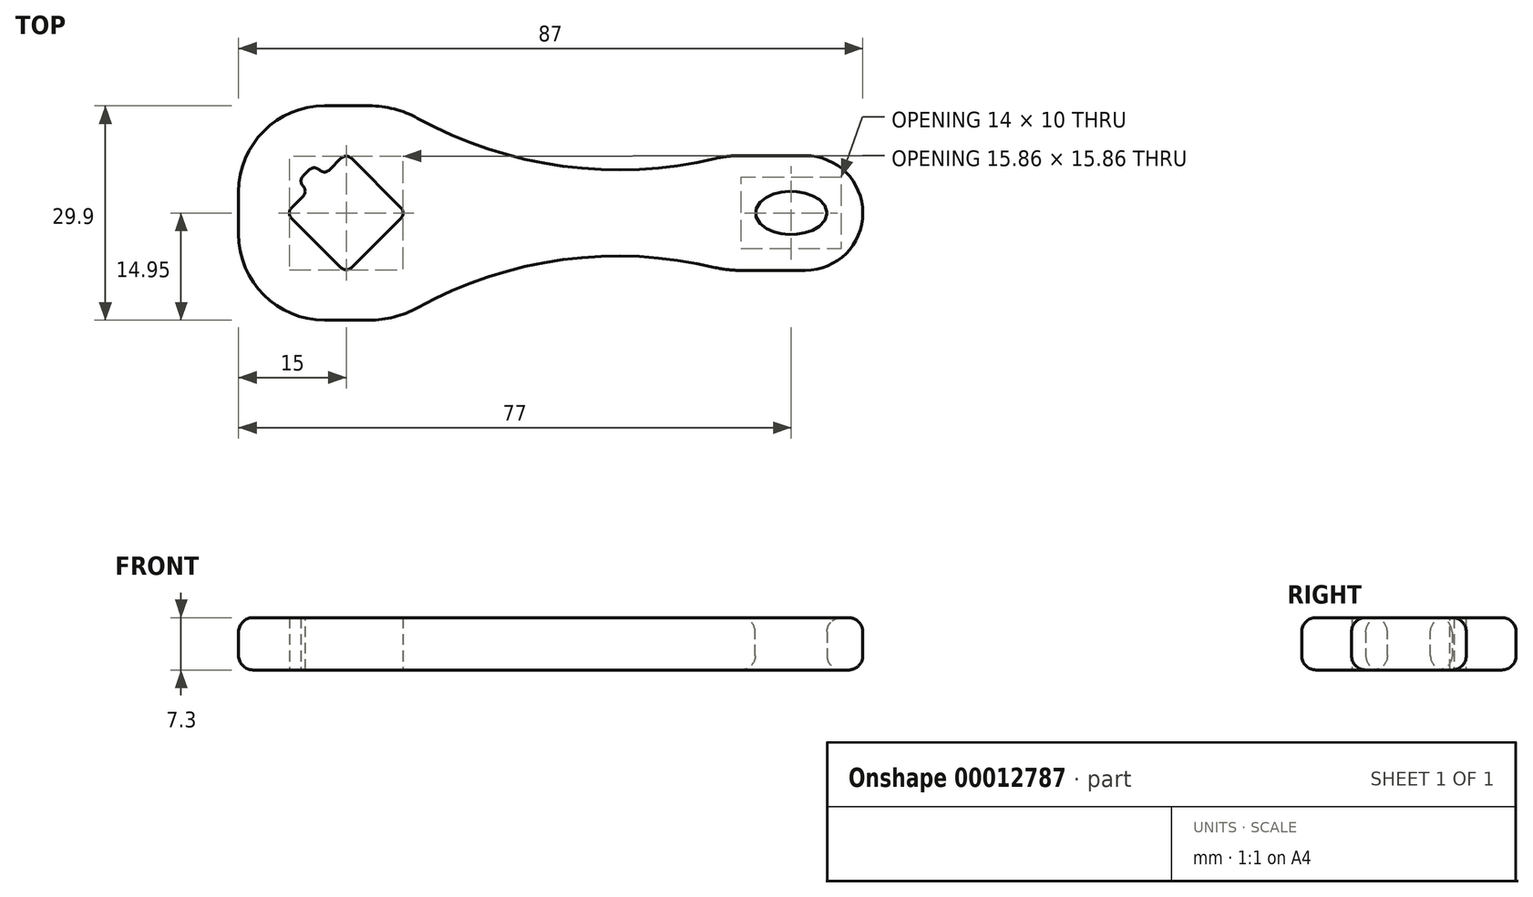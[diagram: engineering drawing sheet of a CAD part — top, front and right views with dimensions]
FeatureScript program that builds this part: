
annotation { "Feature Type Name" : "Feature", "Feature Type Description" : "" }
export const myFeature = defineFeature(function(context is Context, id is Id, definition is map)
    precondition{}
    {
        {
            var Q0;
            Q0=qCreatedBy(makeId("Top.planeOp"),FACE);
            var sketch = newSketch(context, id + "F0", { "sketchPlane" : qUnion([Q0])});
            skLineSegment(sketch, "E0", {"start": v(0, 8.34) * mm, "end": v(0, -8.34) * mm, "construction": true});
            skLineSegment(sketch, "E1", {"start": v(0, 8.34) * mm, "end": v(8.34, 0) * mm});
            skLineSegment(sketch, "E2", {"start": v(8.34, 0) * mm, "end": v(0, -8.34) * mm});
            skLineSegment(sketch, "E3", {"start": v(0, -8.34) * mm, "end": v(-8.34, 0) * mm});
            skLineSegment(sketch, "E4", {"start": v(-8.34, 0) * mm, "end": v(-5.3, 3.04) * mm});
            skLineSegment(sketch, "E5", {"start": v(-5.3, 3.04) * mm, "end": v(-6.72, 4.45) * mm});
            skLineSegment(sketch, "E6", {"start": v(-6.72, 4.45) * mm, "end": v(-4.45, 6.72) * mm});
            skLineSegment(sketch, "E7", {"start": v(-4.45, 6.72) * mm, "end": v(-3.04, 5.3) * mm});
            skLineSegment(sketch, "E8", {"start": v(-3.04, 5.3) * mm, "end": v(0, 8.34) * mm});
            skSolve(sketch);
        }
        {
            var Q0;
            Q0=qCreatedBy(makeId("Top.planeOp"),FACE);
            var sketch = newSketch(context, id + "F1", { "sketchPlane" : qUnion([Q0])});
            skLineSegment(sketch, "E9", {"start": v(7, 14.95) * mm, "end": v(-3, 14.95) * mm});
            skLineSegment(sketch, "E10", {"start": v(-15, 2.95) * mm, "end": v(-15, -2.95) * mm});
            skLineSegment(sketch, "E11", {"start": v(-3, -14.95) * mm, "end": v(7, -14.95) * mm});
            skPoint(sketch, "E12.visualSharp", {"position": v(-15, 14.95) * mm});
            skArc(sketch, "E12.filletArc", {"start": v(-3, 14.95) * mm, "mid": v(-11.49, 11.44) * mm, "end": v(-15, 2.95) * mm});
            skPoint(sketch, "E13.visualSharp", {"position": v(-15, -14.95) * mm});
            skArc(sketch, "E13.filletArc", {"start": v(-15, -2.95) * mm, "mid": v(-11.49, -11.44) * mm, "end": v(-3, -14.95) * mm});
            skLineSegment(sketch, "E14", {"start": v(0, 0) * mm, "end": v(64, 0) * mm, "construction": true});
            skLineSegment(sketch, "E15", {"start": v(0, 0) * mm, "end": v(-15, 0) * mm, "construction": true});
            skLineSegment(sketch, "E16", {"start": v(53, 8) * mm, "end": v(64, 8) * mm});
            skLineSegment(sketch, "E17", {"start": v(53, -8) * mm, "end": v(64, -8) * mm});
            skArc(sketch, "E18", {"start": v(64, 8) * mm, "mid": v(72, 0) * mm, "end": v(64, -8) * mm});
            skArc(sketch, "E19", {"start": v(7, 14.95) * mm, "mid": v(29.27, 6.66) * mm, "end": v(53, 8) * mm});
            skArc(sketch, "E20", {"start": v(53, -8) * mm, "mid": v(29.27, -6.66) * mm, "end": v(7, -14.95) * mm});
            skEllipse(sketch, "E21", {"center": v(62, 0) * mm, "majorRadius": 5 * mm, "minorRadius": 3 * mm, "majorAxis": v(1, 0)});
            skLineSegment(sketch, "E22", {"start": v(62, 8) * mm, "end": v(62, 3) * mm, "construction": true});
            skLineSegment(sketch, "E23", {"start": v(67, 0) * mm, "end": v(72, 0) * mm, "construction": true});
            skSolve(sketch);
        }
        {
            var Q0;
            Q0=qSketchRegion(id+"F0",true);
            extrude(context, id + "F2", {"entities" : qUnion([Q0]), "depth" : 10 * mm});
        }
        {
            var Q0;
            Q0=qSketchRegion(id+"F1",true);
            extrude(context, id + "F3", {"entities" : qUnion([Q0]), "depth" : 7.3 * mm});
        }
        {
            var Q0;
            Q0=makeQuery(id+"F2.opExtrude","SWEPT_EDGE",EDGE,{"disambiguationData":[OSD([sQuery(id+"F0.wireOp",EDGE,"E2"),sQuery(id+"F0.wireOp",EDGE,"E3")])]});
            var Q1;
            Q1=makeQuery(id+"F2.opExtrude","SWEPT_EDGE",EDGE,{"disambiguationData":[OSD([sQuery(id+"F0.wireOp",EDGE,"E3"),sQuery(id+"F0.wireOp",EDGE,"E4")])]});
            var Q2;
            Q2=makeQuery(id+"F2.opExtrude","SWEPT_EDGE",EDGE,{"disambiguationData":[OSD([sQuery(id+"F0.wireOp",EDGE,"E1"),sQuery(id+"F0.wireOp",EDGE,"E2")])]});
            var Q3;
            Q3=makeQuery(id+"F2.opExtrude","SWEPT_EDGE",EDGE,{"disambiguationData":[OSD([sQuery(id+"F0.wireOp",EDGE,"E1"),sQuery(id+"F0.wireOp",EDGE,"E8")])]});
            var Q4;
            Q4=makeQuery(id+"F2.opExtrude","SWEPT_EDGE",EDGE,{"disambiguationData":[OSD([sQuery(id+"F0.wireOp",EDGE,"E6"),sQuery(id+"F0.wireOp",EDGE,"E7")])]});
            var Q5;
            Q5=makeQuery(id+"F2.opExtrude","SWEPT_EDGE",EDGE,{"disambiguationData":[OSD([sQuery(id+"F0.wireOp",EDGE,"E5"),sQuery(id+"F0.wireOp",EDGE,"E6")])]});
            var Q6;
            Q6=makeQuery(id+"F2.opExtrude","SWEPT_EDGE",EDGE,{"disambiguationData":[OSD([sQuery(id+"F0.wireOp",EDGE,"E4"),sQuery(id+"F0.wireOp",EDGE,"E5")])]});
            var Q7;
            Q7=makeQuery(id+"F2.opExtrude","SWEPT_EDGE",EDGE,{"disambiguationData":[OSD([sQuery(id+"F0.wireOp",EDGE,"E7"),sQuery(id+"F0.wireOp",EDGE,"E8")])]});
            fillet(context, id + "F4", {"entities" : qUnion([Q0, Q1, Q2, Q3, Q4, Q5, Q6, Q7]), "radius" : 1 * mm, "allowEdgeOverflow" : false});
        }
        {
            var Q0;
            Q0=makeQuery(id+"F2.opExtrude","SWEPT_BODY",BODY,{"disambiguationData":[OSD([sQuery(id+"F0.wireOp",EDGE,"E1"),sQuery(id+"F0.wireOp",EDGE,"E2"),sQuery(id+"F0.wireOp",EDGE,"E3"),sQuery(id+"F0.wireOp",EDGE,"E4"),sQuery(id+"F0.wireOp",EDGE,"E5"),sQuery(id+"F0.wireOp",EDGE,"E6"),sQuery(id+"F0.wireOp",EDGE,"E7"),sQuery(id+"F0.wireOp",EDGE,"E8")])]});
            var Q1;
            Q1=makeQuery(id+"F3.opExtrude","SWEPT_BODY",BODY,{"disambiguationData":[OSD([sQuery(id+"F1.wireOp",EDGE,"E9"),sQuery(id+"F1.wireOp",EDGE,"E10"),sQuery(id+"F1.wireOp",EDGE,"E11"),sQuery(id+"F1.wireOp",EDGE,"E12.filletArc"),sQuery(id+"F1.wireOp",EDGE,"E13.filletArc"),sQuery(id+"F1.wireOp",EDGE,"E16"),sQuery(id+"F1.wireOp",EDGE,"E17"),sQuery(id+"F1.wireOp",EDGE,"E18"),sQuery(id+"F1.wireOp",EDGE,"E19"),sQuery(id+"F1.wireOp",EDGE,"E20"),sQuery(id+"F1.wireOp",EDGE,"E21")])]});
            booleanBodies(context, id + "F5", {"operationType" : BooleanOperationType.SUBTRACTION, "tools" : qUnion([Q0]), "targets" : qUnion([Q1])});
        }
        {
            var Q0;
            Q0=makeQuery(id+"F3.opExtrude","SWEPT_EDGE",EDGE,{"disambiguationData":[OSD([sQuery(id+"F1.wireOp",EDGE,"E11"),sQuery(id+"F1.wireOp",EDGE,"E20")])]});
            var Q1;
            Q1=makeQuery(id+"F3.opExtrude","SWEPT_EDGE",EDGE,{"disambiguationData":[OSD([sQuery(id+"F1.wireOp",EDGE,"E9"),sQuery(id+"F1.wireOp",EDGE,"E19")])]});
            var Q2;
            Q2=makeQuery(id+"F3.opExtrude","SWEPT_EDGE",EDGE,{"disambiguationData":[OSD([sQuery(id+"F1.wireOp",EDGE,"E17"),sQuery(id+"F1.wireOp",EDGE,"E20")])]});
            var Q3;
            Q3=makeQuery(id+"F3.opExtrude","SWEPT_EDGE",EDGE,{"disambiguationData":[OSD([sQuery(id+"F1.wireOp",EDGE,"E16"),sQuery(id+"F1.wireOp",EDGE,"E19")])]});
            fillet(context, id + "F6", {"entities" : qUnion([Q0, Q1, Q2, Q3]), "radius" : 14 * mm, "tangentPropagation" : true, "allowEdgeOverflow" : false});
        }
        {
            var Q0;
            Q0=makeQuery(id+"F3.opExtrude","CAP_EDGE",EDGE,{"disambiguationData":[OSD([sQuery(id+"F1.wireOp",EDGE,"E21")])],"isStart":false});
            var Q1;
            Q1=makeQuery(id+"F3.opExtrude","CAP_EDGE",EDGE,{"disambiguationData":[OSD([sQuery(id+"F1.wireOp",EDGE,"E21")])],"isStart":true});
            fillet(context, id + "F7", {"entities" : qUnion([Q0, Q1]), "radius" : 2 * mm, "tangentPropagation" : true, "allowEdgeOverflow" : false});
        }
        {
            var Q0;
            Q0=makeQuery(id+"F3.opExtrude","CAP_EDGE",EDGE,{"disambiguationData":[OSD([sQuery(id+"F1.wireOp",EDGE,"E20")])],"isStart":false});
            var Q1;
            Q1=makeQuery(id+"F3.opExtrude","CAP_EDGE",EDGE,{"disambiguationData":[OSD([sQuery(id+"F1.wireOp",EDGE,"E20")])],"isStart":true});
            fillet(context, id + "F8", {"entities" : qUnion([Q0, Q1]), "radius" : 2 * mm, "tangentPropagation" : true, "allowEdgeOverflow" : false});
        }
    });
